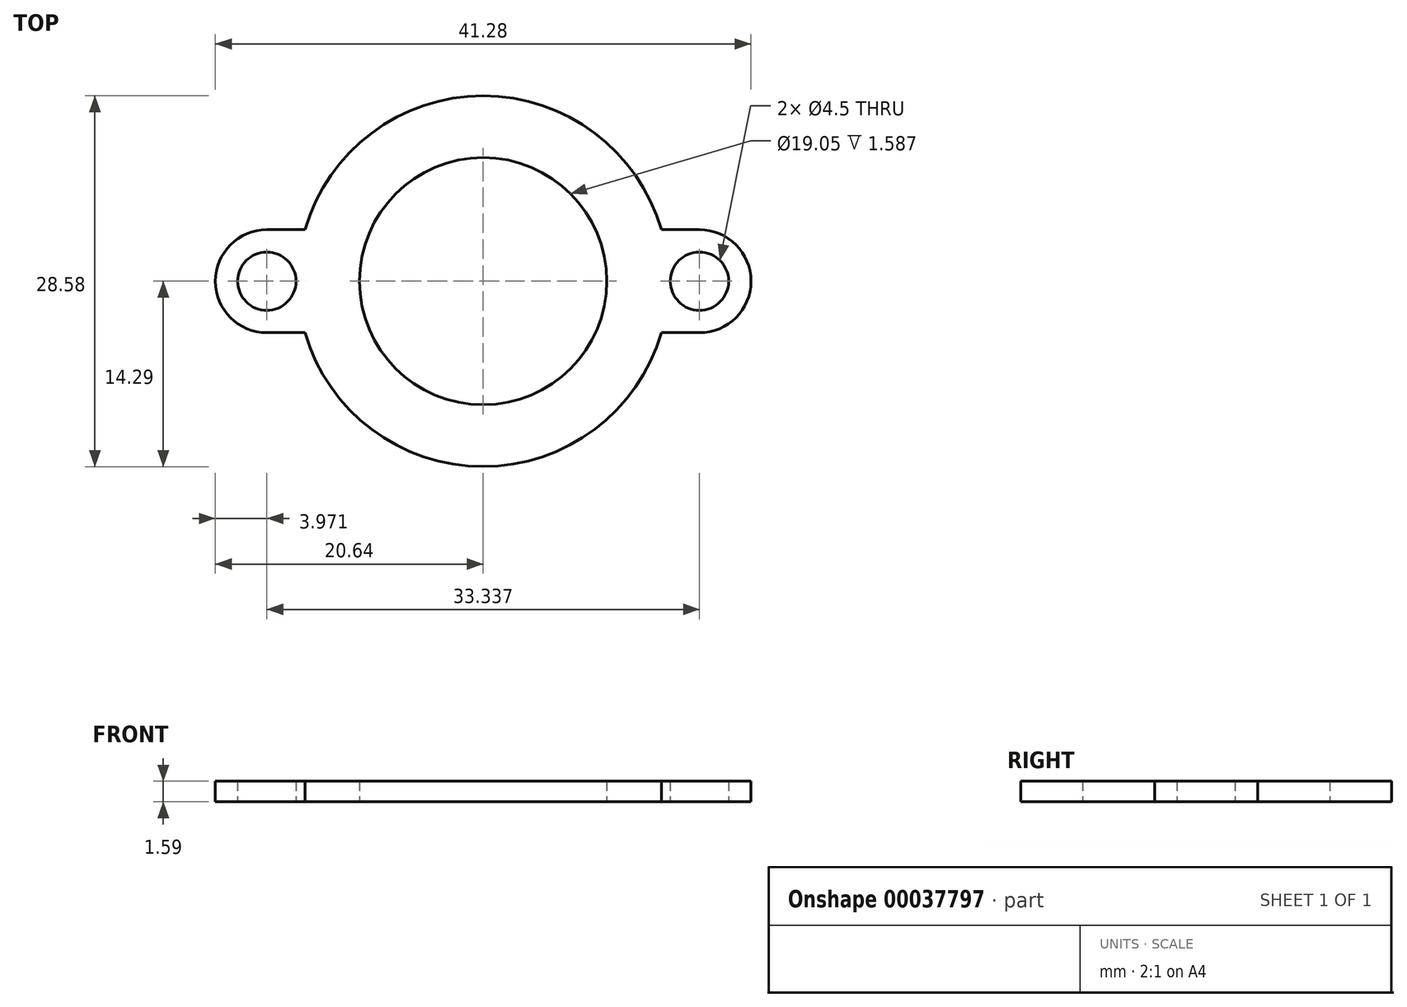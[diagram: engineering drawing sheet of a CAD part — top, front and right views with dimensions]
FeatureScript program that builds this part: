
annotation { "Feature Type Name" : "Feature", "Feature Type Description" : "" }
export const myFeature = defineFeature(function(context is Context, id is Id, definition is map)
    precondition{}
    {
        {
            var Q0;
            Q0=qCreatedBy(makeId("Top.planeOp"),FACE);
            var sketch = newSketch(context, id + "F0", { "sketchPlane" : qUnion([Q0])});
            skCircle(sketch, "E0", {"center": v(0, 0) * mm, "radius": 9.53 * mm});
            skLineSegment(sketch, "E1", {"start": v(-16.67, 0) * mm, "end": v(16.67, 0) * mm, "construction": true});
            skArc(sketch, "E2", {"start": v(13.73, 3.97) * mm, "mid": v(0, 14.29) * mm, "end": v(-13.73, 3.97) * mm});
            skArc(sketch, "E3", {"start": v(-13.73, -3.97) * mm, "mid": v(0, -14.29) * mm, "end": v(13.73, -3.97) * mm});
            skArc(sketch, "E4", {"start": v(-16.67, 3.97) * mm, "mid": v(-20.64, 0) * mm, "end": v(-16.67, -3.97) * mm});
            skArc(sketch, "E5", {"start": v(16.67, -3.97) * mm, "mid": v(20.64, 0) * mm, "end": v(16.67, 3.97) * mm});
            skLineSegment(sketch, "E6", {"start": v(-16.67, 3.97) * mm, "end": v(-16.67, -3.97) * mm, "construction": true});
            skLineSegment(sketch, "E7", {"start": v(16.67, 3.97) * mm, "end": v(16.67, -3.97) * mm, "construction": true});
            skLineSegment(sketch, "E8", {"start": v(16.67, -3.97) * mm, "end": v(13.73, -3.97) * mm});
            skLineSegment(sketch, "E9", {"start": v(16.67, 3.97) * mm, "end": v(13.73, 3.97) * mm});
            skLineSegment(sketch, "E10", {"start": v(-16.67, -3.97) * mm, "end": v(-13.73, -3.97) * mm});
            skLineSegment(sketch, "E11", {"start": v(-16.67, 3.97) * mm, "end": v(-13.73, 3.97) * mm});
            skCircle(sketch, "E12", {"center": v(-16.67, 0) * mm, "radius": 2.25 * mm});
            skCircle(sketch, "E13", {"center": v(16.67, 0) * mm, "radius": 2.25 * mm});
            skSolve(sketch);
        }
        {
            var Q0;
            Q0=qSketchRegion(id+"F0",true);
            extrude(context, id + "F1", {"entities" : qUnion([Q0]), "depth" : 1.59 * mm});
        }
    });
